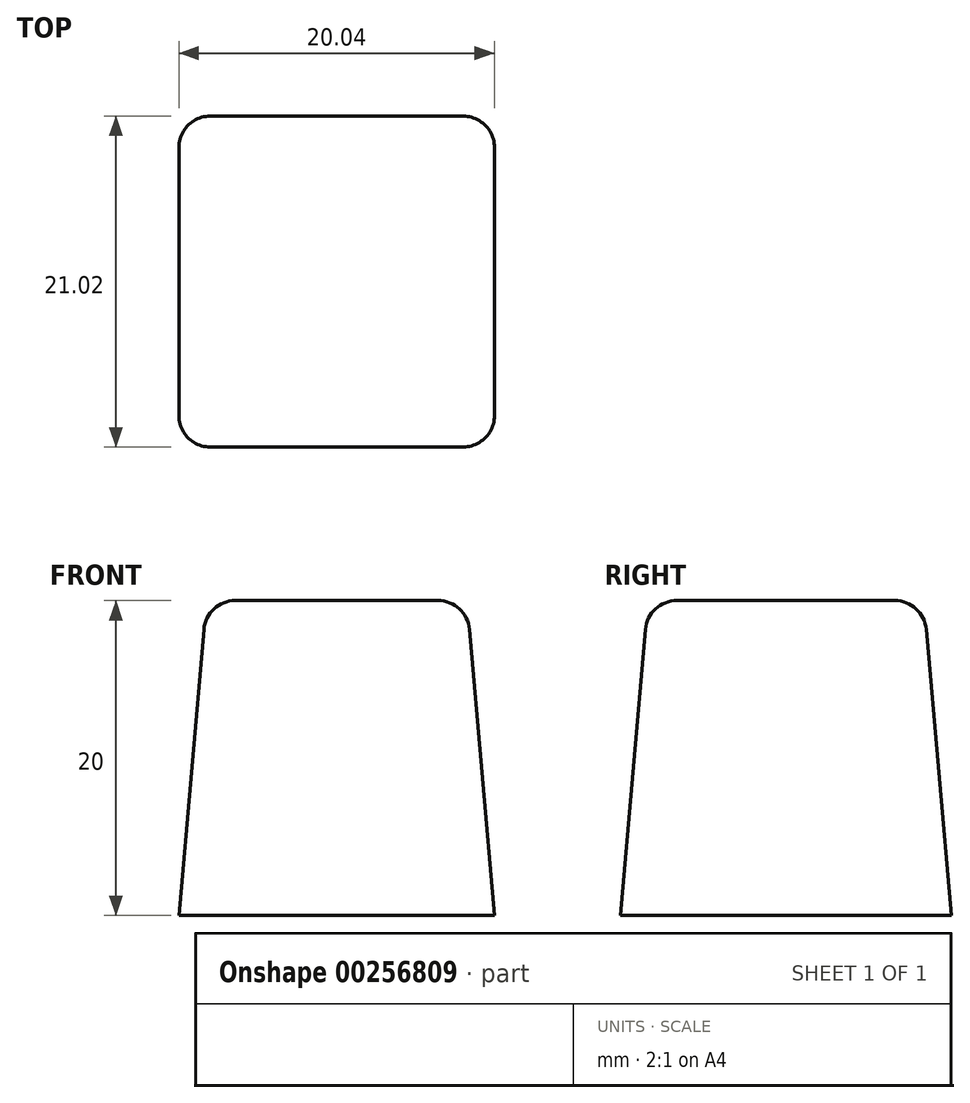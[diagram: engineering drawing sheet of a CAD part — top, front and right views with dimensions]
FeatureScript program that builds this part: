
annotation { "Feature Type Name" : "Feature", "Feature Type Description" : "" }
export const myFeature = defineFeature(function(context is Context, id is Id, definition is map)
    precondition{}
    {
        {
            var Q0;
            Q0=qCreatedBy(makeId("Top.planeOp"),FACE);
            var sketch = newSketch(context, id + "F0", { "sketchPlane" : qUnion([Q0])});
            skLineSegment(sketch, "E0.bottom", {"start": v(10.02, -10.5) * mm, "end": v(-10.02, -10.5) * mm});
            skLineSegment(sketch, "E0.top", {"start": v(10.02, 10.5) * mm, "end": v(-10.02, 10.5) * mm});
            skLineSegment(sketch, "E0.left", {"start": v(10.02, -10.5) * mm, "end": v(10.02, 10.5) * mm});
            skLineSegment(sketch, "E0.right", {"start": v(-10.02, -10.5) * mm, "end": v(-10.02, 10.5) * mm});
            skPoint(sketch, "E0.middle", {"position": v(0, 0) * mm});
            skSolve(sketch);
        }
        {
            var Q0;
            Q0=qSketchRegion(id+"F0",true);
            extrude(context, id + "F1", {"entities" : qUnion([Q0]), "depth" : 20 * mm, "hasDraft" : true, "draftAngle" : 5 * degree, "draftPullDirection" : true});
        }
        {
            var Q0;
            Q0=makeQuery(id+"F1.opExtrude","CAP_EDGE",EDGE,{"disambiguationData":[OSD([sQuery(id+"F0.wireOp",EDGE,"E0.top")])],"isStart":false});
            var Q1;
            Q1=makeQuery(id+"F1.opExtrude","CAP_EDGE",EDGE,{"disambiguationData":[OSD([sQuery(id+"F0.wireOp",EDGE,"E0.right")])],"isStart":false});
            var Q2;
            Q2=makeQuery(id+"F1.opExtrude","CAP_FACE",FACE,{"disambiguationData":[OSD([sQuery(id+"F0.wireOp",EDGE,"E0.bottom"),sQuery(id+"F0.wireOp",EDGE,"E0.top"),sQuery(id+"F0.wireOp",EDGE,"E0.left"),sQuery(id+"F0.wireOp",EDGE,"E0.right")])],"isStart":false});
            var Q3;
            Q3=makeQuery(id+"F1.opExtrude","CAP_EDGE",EDGE,{"disambiguationData":[OSD([sQuery(id+"F0.wireOp",EDGE,"E0.left")])],"isStart":false});
            var Q4;
            Q4=makeQuery(id+"F1.opExtrude","SWEPT_EDGE",EDGE,{"disambiguationData":[OSD([sQuery(id+"F0.wireOp",EDGE,"E0.top"),sQuery(id+"F0.wireOp",EDGE,"E0.left")])]});
            var Q5;
            Q5=makeQuery(id+"F1.opExtrude","SWEPT_EDGE",EDGE,{"disambiguationData":[OSD([sQuery(id+"F0.wireOp",EDGE,"E0.top"),sQuery(id+"F0.wireOp",EDGE,"E0.right")])]});
            var Q6;
            Q6=makeQuery(id+"F1.opExtrude","SWEPT_EDGE",EDGE,{"disambiguationData":[OSD([sQuery(id+"F0.wireOp",EDGE,"E0.bottom"),sQuery(id+"F0.wireOp",EDGE,"E0.left")])]});
            var Q7;
            Q7=makeQuery(id+"F1.opExtrude","SWEPT_EDGE",EDGE,{"disambiguationData":[OSD([sQuery(id+"F0.wireOp",EDGE,"E0.bottom"),sQuery(id+"F0.wireOp",EDGE,"E0.right")])]});
            fillet(context, id + "F2", {"entities" : qUnion([Q0, Q1, Q2, Q3, Q4, Q5, Q6, Q7]), "radius" : 2 * mm, "tangentPropagation" : true, "allowEdgeOverflow" : false});
        }
    });
